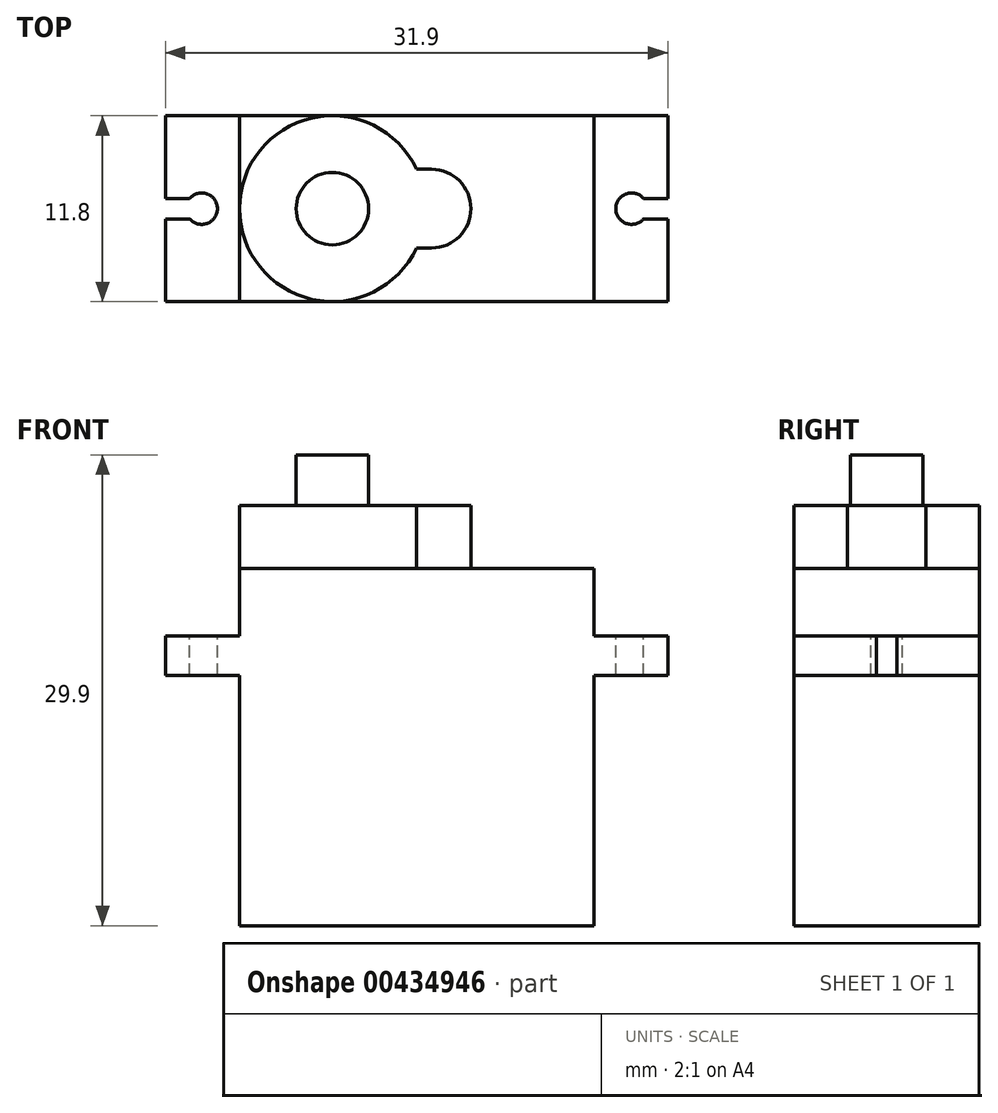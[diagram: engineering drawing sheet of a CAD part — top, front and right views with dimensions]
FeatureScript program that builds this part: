
annotation { "Feature Type Name" : "Feature", "Feature Type Description" : "" }
export const myFeature = defineFeature(function(context is Context, id is Id, definition is map)
    precondition{}
    {
        {
            var Q0;
            Q0=qCreatedBy(makeId("Front.planeOp"),FACE);
            var sketch = newSketch(context, id + "F0", { "sketchPlane" : qUnion([Q0])});
            skLineSegment(sketch, "E0.bottom", {"start": v(11.25, -11.35) * mm, "end": v(-11.25, -11.35) * mm});
            skLineSegment(sketch, "E0.top", {"start": v(11.25, 11.35) * mm, "end": v(-11.25, 11.35) * mm});
            skLineSegment(sketch, "E0.left", {"start": v(11.25, -11.35) * mm, "end": v(11.25, 11.35) * mm});
            skLineSegment(sketch, "E0.right", {"start": v(-11.25, -11.35) * mm, "end": v(-11.25, 11.35) * mm});
            skPoint(sketch, "E0.middle", {"position": v(0, 0) * mm});
            skLineSegment(sketch, "E1.bottom", {"start": v(15.95, 4.55) * mm, "end": v(-15.95, 4.55) * mm});
            skLineSegment(sketch, "E1.top", {"start": v(15.95, 7.05) * mm, "end": v(-15.95, 7.05) * mm});
            skLineSegment(sketch, "E1.left", {"start": v(15.95, 4.55) * mm, "end": v(15.95, 7.05) * mm});
            skLineSegment(sketch, "E1.right", {"start": v(-15.95, 4.55) * mm, "end": v(-15.95, 7.05) * mm});
            skPoint(sketch, "E1.middle", {"position": v(0, 5.8) * mm});
            skSolve(sketch);
        }
        {
            var Q0;
            {var subQ0=sQuery(id+"F0.wireOp",EDGE,"E0.bottom");Q0=makeQuery(id+"F0.imprint","IMPRINT",FACE,{"disambiguationData":[TD([[makeQuery(id+"F0.imprint","IMPRINT",EDGE,{"derivedFrom":subQ0}),-1.0]])]});}
            var Q1;
            {var subQ0=sQuery(id+"F0.wireOp",EDGE,"E1.bottom");var subQ1=sQuery(id+"F0.wireOp",EDGE,"E0.left");var subQ2=makeQuery(id+"F0.imprint","INTERSECT",VERTEX,{"derivedFrom":[subQ1,subQ0]});Q1=makeQuery(id+"F0.imprint","IMPRINT",FACE,{"disambiguationData":[TD([[makeQuery(id+"F0.imprint","IMPRINT",EDGE,{"disambiguationData":[TD([[subQ2,-1.0]])],"derivedFrom":subQ1}),1.0]])]});}
            var Q2;
            {var subQ5=sQuery(id+"F0.wireOp",EDGE,"E1.left");Q2=makeQuery(id+"F0.imprint","IMPRINT",FACE,{"disambiguationData":[TD([[makeQuery(id+"F0.imprint","IMPRINT",EDGE,{"derivedFrom":subQ5}),1.0]])]});}
            var Q3;
            {var subQ5=sQuery(id+"F0.wireOp",EDGE,"E1.right");Q3=makeQuery(id+"F0.imprint","IMPRINT",FACE,{"disambiguationData":[TD([[makeQuery(id+"F0.imprint","IMPRINT",EDGE,{"derivedFrom":subQ5}),-1.0]])]});}
            var Q4;
            {var subQ0=sQuery(id+"F0.wireOp",EDGE,"E0.top");Q4=makeQuery(id+"F0.imprint","IMPRINT",FACE,{"disambiguationData":[TD([[makeQuery(id+"F0.imprint","IMPRINT",EDGE,{"derivedFrom":subQ0}),1.0]])]});}
            extrude(context, id + "F1", {"entities" : qUnion([Q0, Q1, Q2, Q3, Q4]), "endBound" : BoundingType.SYMMETRIC, "depth" : 11.8 * mm});
        }
        {
            var Q0;
            Q0=makeQuery(id+"F1.opExtrude","SWEPT_FACE",FACE,{"disambiguationData":[OSD([sQuery(id+"F0.wireOp",EDGE,"E0.top")])]});
            var sketch = newSketch(context, id + "F2", { "sketchPlane" : qUnion([Q0])});
            skCircle(sketch, "E2", {"center": v(-5.35, 0) * mm, "radius": 5.9 * mm});
            skLineSegment(sketch, "E3", {"start": v(0.95, 2.5) * mm, "end": v(-5.35, 2.5) * mm});
            skLineSegment(sketch, "E4", {"start": v(-5.35, -2.5) * mm, "end": v(0.95, -2.5) * mm});
            skArc(sketch, "E5", {"start": v(0.95, -2.5) * mm, "mid": v(3.45, 0) * mm, "end": v(0.95, 2.5) * mm});
            skSolve(sketch);
        }
        {
            var Q0;
            {var subQ0=sQuery(id+"F2.wireOp",EDGE,"E2");var subQ6=makeQuery(id+"F2.imprint","INTERSECT",VERTEX,{"derivedFrom":[subQ0,sQuery(id+"F2.wireOp",EDGE,"E3")]});Q0=makeQuery(id+"F2.imprint","IMPRINT",FACE,{"disambiguationData":[TD([[makeQuery(id+"F2.imprint","IMPRINT",EDGE,{"disambiguationData":[TD([[subQ6,-1.0]])],"derivedFrom":subQ0}),1.0]])]});}
            var Q1;
            {var subQ5=sQuery(id+"F2.wireOp",EDGE,"E5");Q1=makeQuery(id+"F2.imprint","IMPRINT",FACE,{"disambiguationData":[TD([[makeQuery(id+"F2.imprint","IMPRINT",EDGE,{"derivedFrom":subQ5}),1.0]])]});}
            extrude(context, id + "F3", {"entities" : qUnion([Q0, Q1]), "operationType" : NewBodyOperationType.ADD, "depth" : 4 * mm});
        }
        {
            var Q0;
            {var subQ0=sQuery(id+"F0.wireOp",EDGE,"E1.top");Q0=makeQuery(id+"F1.opExtrude","SWEPT_FACE",FACE,{"disambiguationData":[OSD([subQ0]),TDD([makeQuery(id+"F0.imprint","IMPRINT",EDGE,{"disambiguationData":[TD([[makeQuery(id+"F0.imprint","INTERSECT",VERTEX,{"derivedFrom":[subQ0,sQuery(id+"F0.wireOp",EDGE,"E1.left")]}),-1.0]])],"derivedFrom":subQ0})])]});}
            var sketch = newSketch(context, id + "F4", { "sketchPlane" : qUnion([Q0])});
            skCircle(sketch, "E6", {"center": v(13.65, 0) * mm, "radius": 1 * mm});
            skLineSegment(sketch, "E7", {"start": v(14.4, 0.65) * mm, "end": v(15.95, 0.65) * mm});
            skLineSegment(sketch, "E8", {"start": v(14.4, -0.65) * mm, "end": v(15.95, -0.65) * mm});
            skSolve(sketch);
        }
        {
            var Q0;
            {var subQ0=sQuery(id+"F4.wireOp",EDGE,"E6");var subQ1=makeQuery(id+"F4.imprint","INTERSECT",VERTEX,{"derivedFrom":[subQ0,sQuery(id+"F4.wireOp",EDGE,"E7")]});Q0=makeQuery(id+"F4.imprint","IMPRINT",FACE,{"disambiguationData":[TD([[makeQuery(id+"F4.imprint","IMPRINT",EDGE,{"disambiguationData":[TD([[subQ1,-1.0]])],"derivedFrom":subQ0}),1.0]])]});}
            var Q1;
            {var subQ0=sQuery(id+"F4.wireOp",EDGE,"E7");Q1=makeQuery(id+"F4.imprint","IMPRINT",FACE,{"disambiguationData":[TD([[makeQuery(id+"F4.imprint","IMPRINT",EDGE,{"derivedFrom":subQ0}),-1.0]])]});}
            extrude(context, id + "F5", {"entities" : qUnion([Q0, Q1]), "operationType" : NewBodyOperationType.REMOVE, "endBound" : BoundingType.THROUGH_ALL, "oppositeDirection" : true, "depth" : 25 * mm});
        }
        {
            var Q0;
            {var subQ0=sQuery(id+"F0.wireOp",EDGE,"E1.top");Q0=makeQuery(id+"F1.opExtrude","SWEPT_FACE",FACE,{"disambiguationData":[OSD([subQ0]),TDD([makeQuery(id+"F0.imprint","IMPRINT",EDGE,{"disambiguationData":[TD([[makeQuery(id+"F0.imprint","INTERSECT",VERTEX,{"derivedFrom":[subQ0,sQuery(id+"F0.wireOp",EDGE,"E1.right")]}),1.0]])],"derivedFrom":subQ0})])]});}
            var sketch = newSketch(context, id + "F6", { "sketchPlane" : qUnion([Q0])});
            skCircle(sketch, "E9", {"center": v(-13.65, 0) * mm, "radius": 1 * mm});
            skLineSegment(sketch, "E10", {"start": v(-14.4, 0.65) * mm, "end": v(-15.95, 0.65) * mm});
            skLineSegment(sketch, "E11", {"start": v(-14.4, -0.65) * mm, "end": v(-15.95, -0.65) * mm});
            skSolve(sketch);
        }
        {
            var Q0;
            {var subQ0=sQuery(id+"F6.wireOp",EDGE,"E9");var subQ1=makeQuery(id+"F6.imprint","INTERSECT",VERTEX,{"derivedFrom":[subQ0,sQuery(id+"F6.wireOp",EDGE,"E10")]});Q0=makeQuery(id+"F6.imprint","IMPRINT",FACE,{"disambiguationData":[TD([[makeQuery(id+"F6.imprint","IMPRINT",EDGE,{"disambiguationData":[TD([[subQ1,-1.0]])],"derivedFrom":subQ0}),1.0]])]});}
            var Q1;
            {var subQ0=sQuery(id+"F6.wireOp",EDGE,"E10");Q1=makeQuery(id+"F6.imprint","IMPRINT",FACE,{"disambiguationData":[TD([[makeQuery(id+"F6.imprint","IMPRINT",EDGE,{"derivedFrom":subQ0}),1.0]])]});}
            extrude(context, id + "F7", {"entities" : qUnion([Q0, Q1]), "operationType" : NewBodyOperationType.REMOVE, "oppositeDirection" : true, "depth" : 25 * mm});
        }
        {
            var Q0;
            Q0=makeQuery(id+"F3.opExtrude","CAP_FACE",FACE,{"disambiguationData":[OSD([sQuery(id+"F2.wireOp",EDGE,"E2"),sQuery(id+"F2.wireOp",EDGE,"E3"),sQuery(id+"F2.wireOp",EDGE,"E4"),sQuery(id+"F2.wireOp",EDGE,"E5")])],"isStart":false});
            var sketch = newSketch(context, id + "F8", { "sketchPlane" : qUnion([Q0])});
            skCircle(sketch, "E12", {"center": v(-5.35, 0) * mm, "radius": 2.3 * mm});
            skSolve(sketch);
        }
        {
            var Q0;
            Q0=makeQuery(id+"F8.imprint","IMPRINT",FACE,{"disambiguationData":[TD([[makeQuery(id+"F8.imprint","IMPRINT",EDGE,{"derivedFrom":sQuery(id+"F8.wireOp",EDGE,"E12")}),1.0]])]});
            extrude(context, id + "F9", {"entities" : qUnion([Q0]), "operationType" : NewBodyOperationType.ADD, "depth" : 3.2 * mm});
        }
    });
